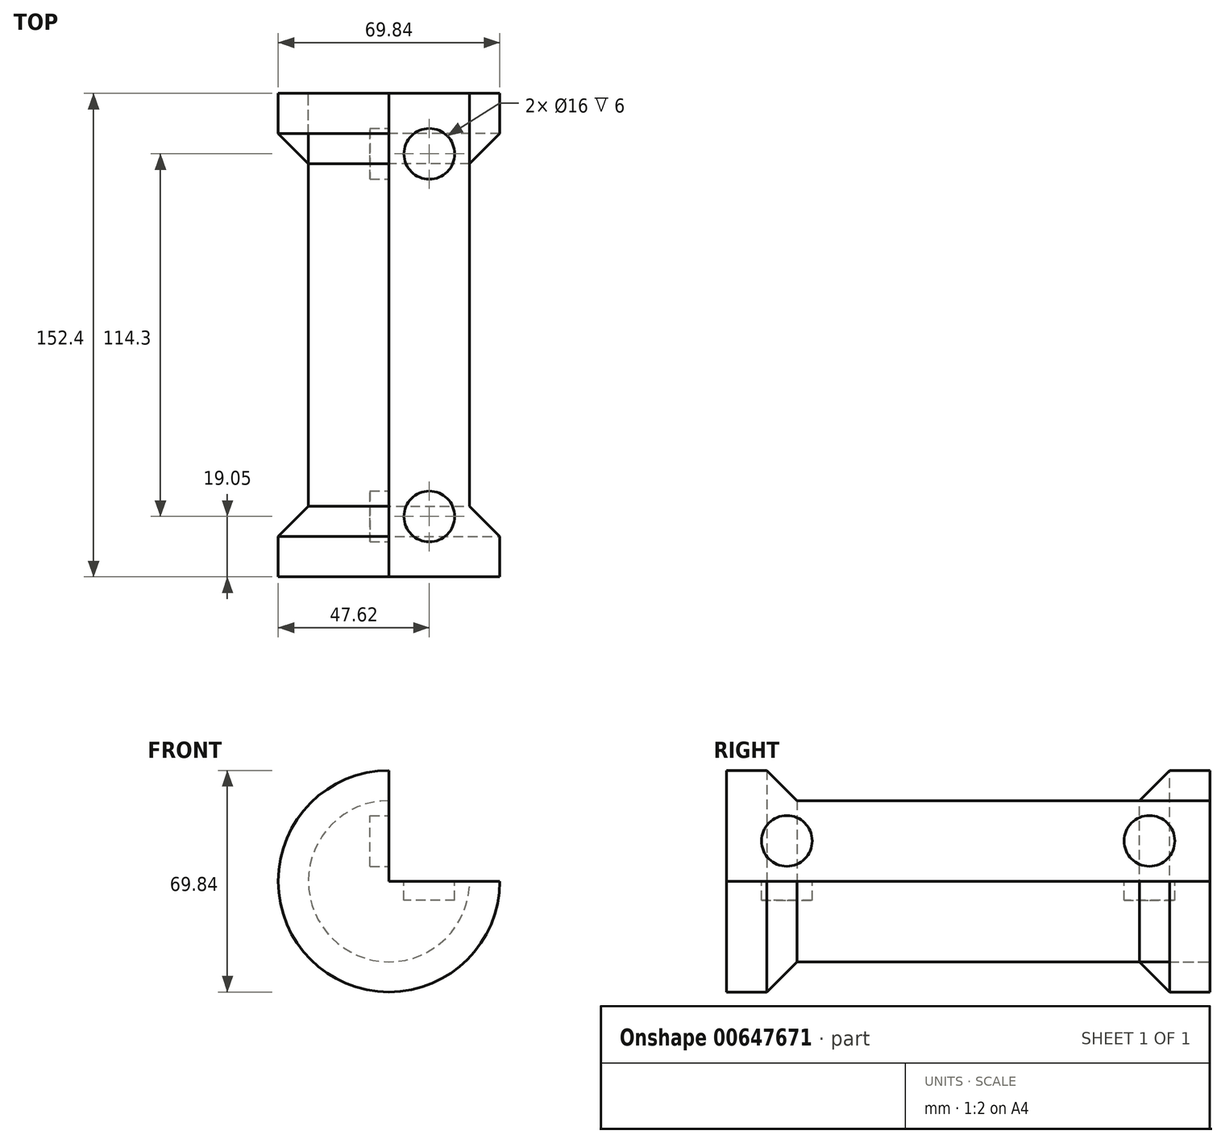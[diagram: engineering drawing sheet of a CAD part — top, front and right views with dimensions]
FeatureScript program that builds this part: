
annotation { "Feature Type Name" : "Feature", "Feature Type Description" : "" }
export const myFeature = defineFeature(function(context is Context, id is Id, definition is map)
    precondition{}
    {
        {
            var Q0;
            Q0=qCreatedBy(makeId("Front.planeOp"),FACE);
            var sketch = newSketch(context, id + "F0", { "sketchPlane" : qUnion([Q0])});
            skCircle(sketch, "E0", {"center": v(0, 0) * mm, "radius": 25.4 * mm});
            skSolve(sketch);
        }
        {
            var Q0;
            Q0=makeQuery(id+"F0.imprint","IMPRINT",FACE,{"disambiguationData":[TD([[makeQuery(id+"F0.imprint","IMPRINT",EDGE,{"derivedFrom":sQuery(id+"F0.wireOp",EDGE,"E0")}),1.0]])]});
            extrude(context, id + "F1", {"entities" : qUnion([Q0]), "endBound" : BoundingType.SYMMETRIC, "depth" : 152.4 * mm, "offsetDistance" : 25.4 * mm});
        }
        {
            var Q0;
            Q0=makeQuery(id+"F1.opExtrude","CAP_FACE",FACE,{"disambiguationData":[OSD([sQuery(id+"F0.wireOp",EDGE,"E0")])],"isStart":false});
            var sketch = newSketch(context, id + "F2", { "sketchPlane" : qUnion([Q0])});
            skCircle(sketch, "E1", {"center": v(0, 0) * mm, "radius": 34.93 * mm});
            skSolve(sketch);
        }
        {
            var Q0;
            Q0=makeQuery(id+"F1.opExtrude","CAP_FACE",FACE,{"disambiguationData":[OSD([sQuery(id+"F0.wireOp",EDGE,"E0")])],"isStart":true});
            var sketch = newSketch(context, id + "F3", { "sketchPlane" : qUnion([Q0])});
            skCircle(sketch, "E2", {"center": v(0, 0) * mm, "radius": 34.93 * mm});
            skSolve(sketch);
        }
        {
            var Q0;
            Q0=makeQuery(id+"F2.imprint","IMPRINT",FACE,{"disambiguationData":[TD([[makeQuery(id+"F2.imprint","IMPRINT",EDGE,{"derivedFrom":sQuery(id+"F2.wireOp",EDGE,"E1")}),1.0]])]});
            extrude(context, id + "F4", {"entities" : qUnion([Q0]), "operationType" : NewBodyOperationType.ADD, "oppositeDirection" : true, "depth" : 25.4 * mm, "offsetDistance" : 25.4 * mm});
        }
        {
            var Q0;
            Q0=makeQuery(id+"F3.imprint","IMPRINT",FACE,{"disambiguationData":[TD([[makeQuery(id+"F3.imprint","IMPRINT",EDGE,{"derivedFrom":sQuery(id+"F3.wireOp",EDGE,"E2")}),1.0]])]});
            extrude(context, id + "F5", {"entities" : qUnion([Q0]), "oppositeDirection" : true, "depth" : 25.4 * mm, "offsetDistance" : 25.4 * mm});
        }
        {
            var Q0;
            Q0=makeQuery(id+"F5.opExtrude","CAP_EDGE",EDGE,{"disambiguationData":[OSD([sQuery(id+"F3.wireOp",EDGE,"E2")])],"isStart":false});
            var Q1;
            Q1=makeQuery(id+"F4.opExtrude","CAP_EDGE",EDGE,{"disambiguationData":[OSD([sQuery(id+"F2.wireOp",EDGE,"E1")])],"isStart":false});
            chamfer(context, id + "F6", {"entities" : qUnion([Q0, Q1]), "width" : 12.7 * mm, "tangentPropagation" : true});
        }
        {
            var Q0;
            Q0=qCreatedBy(makeId("Front.planeOp"),FACE);
            var sketch = newSketch(context, id + "F7", { "sketchPlane" : qUnion([Q0])});
            skLineSegment(sketch, "E3.bottom", {"start": v(0, 0) * mm, "end": v(48.06, 0) * mm});
            skLineSegment(sketch, "E3.top", {"start": v(0, 48.63) * mm, "end": v(48.06, 48.63) * mm});
            skLineSegment(sketch, "E3.left", {"start": v(0, 0) * mm, "end": v(0, 48.63) * mm});
            skLineSegment(sketch, "E3.right", {"start": v(48.06, 0) * mm, "end": v(48.06, 48.63) * mm});
            skSolve(sketch);
        }
        {
            var Q0;
            Q0=makeQuery(id+"F7.imprint","IMPRINT",FACE,{"disambiguationData":[TD([[makeQuery(id+"F7.imprint","IMPRINT",EDGE,{"derivedFrom":sQuery(id+"F7.wireOp",EDGE,"E3.bottom")}),1.0]])]});
            extrude(context, id + "F8", {"entities" : qUnion([Q0]), "operationType" : NewBodyOperationType.REMOVE, "endBound" : BoundingType.SYMMETRIC, "oppositeDirection" : true, "depth" : 177.8 * mm, "offsetDistance" : 25.4 * mm});
        }
        {
            var Q0;
            {var subQ0=sQuery(id+"F0.wireOp",EDGE,"E0");Q0=makeQuery(id+"F8.boolean.opBoolean","COPY",FACE,{"disambiguationData":[TD([makeQuery(id+"F1.opExtrude","SWEPT_FACE",FACE,{"disambiguationData":[OSD([subQ0])]})])],"derivedFrom":makeQuery(id+"F8.opExtrude","SWEPT_FACE",FACE,{"disambiguationData":[OSD([sQuery(id+"F7.wireOp",EDGE,"E3.left")])]})});}
            var sketch = newSketch(context, id + "F9", { "sketchPlane" : qUnion([Q0])});
            skCircle(sketch, "E4", {"center": v(-57.15, 12.7) * mm, "radius": 8 * mm});
            skCircle(sketch, "E5", {"center": v(57.15, 12.7) * mm, "radius": 8 * mm});
            skSolve(sketch);
        }
        {
            var Q0;
            Q0=makeQuery(id+"F9.imprint","IMPRINT",FACE,{"disambiguationData":[TD([[makeQuery(id+"F9.imprint","IMPRINT",EDGE,{"derivedFrom":sQuery(id+"F9.wireOp",EDGE,"E4")}),1.0]])]});
            var Q1;
            Q1=makeQuery(id+"F9.imprint","IMPRINT",FACE,{"disambiguationData":[TD([[makeQuery(id+"F9.imprint","IMPRINT",EDGE,{"derivedFrom":sQuery(id+"F9.wireOp",EDGE,"E5")}),1.0]])]});
            extrude(context, id + "F10", {"entities" : qUnion([Q0, Q1]), "operationType" : NewBodyOperationType.REMOVE, "oppositeDirection" : true, "depth" : 6 * mm, "offsetDistance" : 25.4 * mm});
        }
        {
            var Q0;
            {var subQ0=sQuery(id+"F0.wireOp",EDGE,"E0");Q0=makeQuery(id+"F8.boolean.opBoolean","COPY",FACE,{"disambiguationData":[TD([makeQuery(id+"F1.opExtrude","SWEPT_FACE",FACE,{"disambiguationData":[OSD([subQ0])]})])],"derivedFrom":makeQuery(id+"F8.opExtrude","SWEPT_FACE",FACE,{"disambiguationData":[OSD([sQuery(id+"F7.wireOp",EDGE,"E3.bottom")])]})});}
            var sketch = newSketch(context, id + "F11", { "sketchPlane" : qUnion([Q0])});
            skCircle(sketch, "E6", {"center": v(12.7, -57.15) * mm, "radius": 8 * mm});
            skCircle(sketch, "E7", {"center": v(12.7, 57.15) * mm, "radius": 8 * mm});
            skSolve(sketch);
        }
        {
            var Q0;
            Q0 = qSketchRegion(id + "F11", true);
            extrude(context, id + "F12", {"entities" : qUnion([Q0]), "operationType" : NewBodyOperationType.REMOVE, "oppositeDirection" : true, "depth" : 6 * mm, "offsetDistance" : 25.4 * mm});
        }
    });
